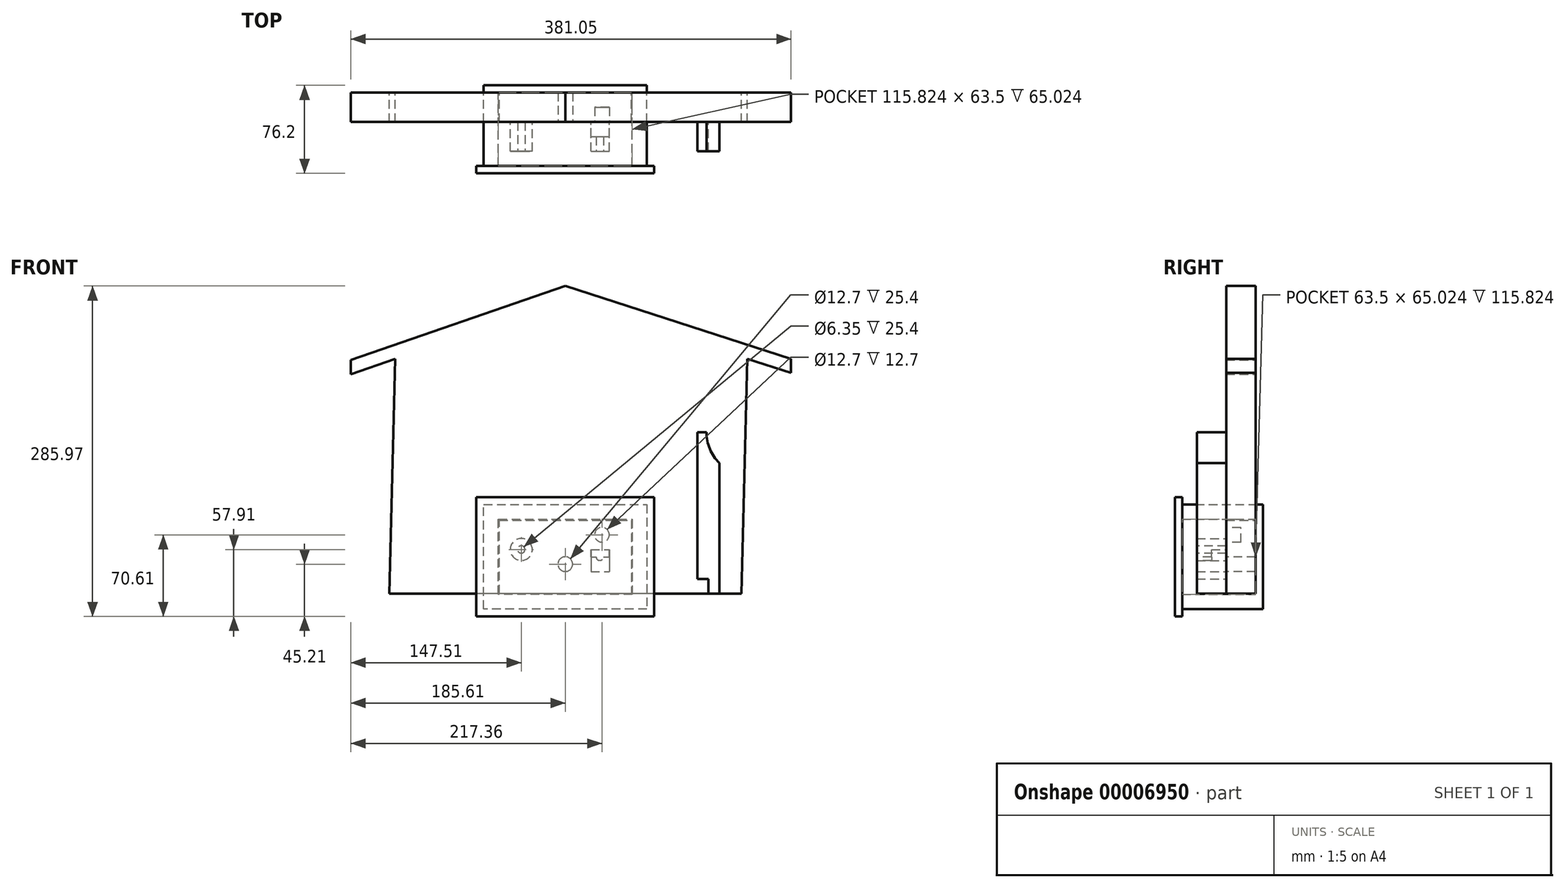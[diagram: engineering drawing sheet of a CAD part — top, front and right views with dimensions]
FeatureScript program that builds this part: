
annotation { "Feature Type Name" : "Feature", "Feature Type Description" : "" }
export const myFeature = defineFeature(function(context is Context, id is Id, definition is map)
    precondition{}
    {
        {
            var Q0;
            Q0=qCreatedBy(makeId("Front.planeOp"),FACE);
            var sketch = newSketch(context, id + "F0", { "sketchPlane" : qUnion([Q0])});
            skLineSegment(sketch, "E0", {"start": v(-57.15, 63.5) * mm, "end": v(57.15, 63.5) * mm});
            skLineSegment(sketch, "E1", {"start": v(57.15, 63.5) * mm, "end": v(57.15, 0) * mm});
            skLineSegment(sketch, "E2", {"start": v(57.15, 0) * mm, "end": v(-57.15, 0) * mm});
            skLineSegment(sketch, "E3", {"start": v(-57.15, 0) * mm, "end": v(-57.15, 63.5) * mm});
            skSolve(sketch);
        }
        {
            var Q0;
            Q0=makeQuery(id+"F0.imprint","IMPRINT",FACE,{"disambiguationData":[TD([[makeQuery(id+"F0.imprint","IMPRINT",EDGE,{"derivedFrom":sQuery(id+"F0.wireOp",EDGE,"E0")}),-1.0]])]});
            extrude(context, id + "F1", {"entities" : qUnion([Q0]), "depth" : 25.4 * mm});
        }
        {
            var Q0;
            Q0=makeQuery(id+"F1.opExtrude","CAP_FACE",FACE,{"disambiguationData":[OSD([sQuery(id+"F0.wireOp",EDGE,"E0"),sQuery(id+"F0.wireOp",EDGE,"E1"),sQuery(id+"F0.wireOp",EDGE,"E2"),sQuery(id+"F0.wireOp",EDGE,"E3")])],"isStart":false});
            var sketch = newSketch(context, id + "F2", { "sketchPlane" : qUnion([Q0])});
            skCircle(sketch, "E4", {"center": v(0, 25.4) * mm, "radius": 6.35 * mm});
            skSolve(sketch);
        }
        {
            var Q0;
            Q0 = qSketchRegion(id + "F2", true);
            extrude(context, id + "F3", {"entities" : qUnion([Q0]), "operationType" : NewBodyOperationType.REMOVE, "endBound" : BoundingType.UP_TO_NEXT, "oppositeDirection" : true, "depth" : 25.4 * mm});
        }
        {
            var Q0;
            Q0=makeQuery(id+"F1.opExtrude","CAP_FACE",FACE,{"disambiguationData":[OSD([sQuery(id+"F0.wireOp",EDGE,"E0"),sQuery(id+"F0.wireOp",EDGE,"E1"),sQuery(id+"F0.wireOp",EDGE,"E2"),sQuery(id+"F0.wireOp",EDGE,"E3")])],"isStart":false});
            var sketch = newSketch(context, id + "F4", { "sketchPlane" : qUnion([Q0])});
            skCircle(sketch, "E5", {"center": v(-38.1, 38.1) * mm, "radius": 9.53 * mm});
            skSolve(sketch);
        }
        {
            var Q0;
            Q0 = qSketchRegion(id + "F4", true);
            extrude(context, id + "F5", {"entities" : qUnion([Q0]), "operationType" : NewBodyOperationType.ADD, "depth" : 25.4 * mm});
        }
        {
            var Q0;
            Q0=makeQuery(id+"F1.opExtrude","CAP_FACE",FACE,{"disambiguationData":[OSD([sQuery(id+"F0.wireOp",EDGE,"E0"),sQuery(id+"F0.wireOp",EDGE,"E1"),sQuery(id+"F0.wireOp",EDGE,"E2"),sQuery(id+"F0.wireOp",EDGE,"E3")])],"isStart":false});
            var sketch = newSketch(context, id + "F6", { "sketchPlane" : qUnion([Q0])});
            skLineSegment(sketch, "E6.bottom", {"start": v(22.22, 38.1) * mm, "end": v(38.1, 38.1) * mm});
            skLineSegment(sketch, "E6.top", {"start": v(22.22, 19.05) * mm, "end": v(38.1, 19.05) * mm});
            skLineSegment(sketch, "E6.left", {"start": v(22.22, 38.1) * mm, "end": v(22.22, 19.05) * mm});
            skLineSegment(sketch, "E6.right", {"start": v(38.1, 38.1) * mm, "end": v(38.1, 19.05) * mm});
            skSolve(sketch);
        }
        {
            var Q0;
            Q0 = qSketchRegion(id + "F6", true);
            extrude(context, id + "F7", {"entities" : qUnion([Q0]), "depth" : 25.4 * mm});
        }
        {
            var Q0;
            Q0=makeQuery(id+"F5.opExtrude","CAP_FACE",FACE,{"disambiguationData":[OSD([sQuery(id+"F4.wireOp",EDGE,"E5")])],"isStart":false});
            var sketch = newSketch(context, id + "F8", { "sketchPlane" : qUnion([Q0])});
            skCircle(sketch, "E7", {"center": v(-38.1, 38.1) * mm, "radius": 3.18 * mm});
            skSolve(sketch);
        }
        {
            var Q0;
            Q0 = qSketchRegion(id + "F8", true);
            extrude(context, id + "F9", {"entities" : qUnion([Q0]), "operationType" : NewBodyOperationType.REMOVE, "oppositeDirection" : true, "depth" : 25.4 * mm});
        }
        {
            var Q0;
            Q0=makeQuery(id+"F1.opExtrude","CAP_FACE",FACE,{"disambiguationData":[OSD([sQuery(id+"F0.wireOp",EDGE,"E0"),sQuery(id+"F0.wireOp",EDGE,"E1"),sQuery(id+"F0.wireOp",EDGE,"E2"),sQuery(id+"F0.wireOp",EDGE,"E3")])],"isStart":true});
            var sketch = newSketch(context, id + "F10", { "sketchPlane" : qUnion([Q0])});
            skLineSegment(sketch, "E8.0", {"start": v(57.91, 64.26) * mm, "end": v(-57.91, 64.26) * mm});
            skLineSegment(sketch, "E8.1", {"start": v(57.91, -0.76) * mm, "end": v(57.91, 64.26) * mm});
            skLineSegment(sketch, "E8.2", {"start": v(-57.91, -0.76) * mm, "end": v(57.91, -0.76) * mm});
            skLineSegment(sketch, "E8.3", {"start": v(-57.91, 64.26) * mm, "end": v(-57.91, -0.76) * mm});
            skLineSegment(sketch, "E9.0", {"start": v(70.61, 76.96) * mm, "end": v(-70.61, 76.96) * mm});
            skLineSegment(sketch, "E9.1", {"start": v(70.61, -13.46) * mm, "end": v(70.61, 76.96) * mm});
            skLineSegment(sketch, "E9.2", {"start": v(-70.61, -13.46) * mm, "end": v(70.61, -13.46) * mm});
            skLineSegment(sketch, "E9.3", {"start": v(-70.61, 76.96) * mm, "end": v(-70.61, -13.46) * mm});
            skSolve(sketch);
        }
        {
            var Q0;
            Q0=makeQuery(id+"F10.imprint","IMPRINT",FACE,{"disambiguationData":[TD([[makeQuery(id+"F10.imprint","IMPRINT",EDGE,{"derivedFrom":sQuery(id+"F10.wireOp",EDGE,"E8.0")}),-1.0]])]});
            extrude(context, id + "F11", {"entities" : qUnion([Q0]), "oppositeDirection" : true, "depth" : 63.5 * mm});
        }
        {
            var Q0;
            Q0=makeQuery(id+"F11.opExtrude","CAP_FACE",FACE,{"disambiguationData":[OSD([sQuery(id+"F10.wireOp",EDGE,"E8.0"),sQuery(id+"F10.wireOp",EDGE,"E8.1"),sQuery(id+"F10.wireOp",EDGE,"E8.2"),sQuery(id+"F10.wireOp",EDGE,"E8.3"),sQuery(id+"F10.wireOp",EDGE,"E9.0"),sQuery(id+"F10.wireOp",EDGE,"E9.1"),sQuery(id+"F10.wireOp",EDGE,"E9.2"),sQuery(id+"F10.wireOp",EDGE,"E9.3")])],"isStart":true});
            extrude(context, id + "F12", {"entities" : qUnion([Q0]), "operationType" : NewBodyOperationType.ADD, "depth" : 6.35 * mm});
        }
        {
            var Q0;
            Q0=makeQuery(id+"F12.opExtrude","CAP_FACE",FACE,{"disambiguationData":[OSD([sQuery(id+"F10.wireOp",EDGE,"E8.0"),sQuery(id+"F10.wireOp",EDGE,"E8.1"),sQuery(id+"F10.wireOp",EDGE,"E8.2"),sQuery(id+"F10.wireOp",EDGE,"E8.3"),sQuery(id+"F10.wireOp",EDGE,"E9.0"),sQuery(id+"F10.wireOp",EDGE,"E9.1"),sQuery(id+"F10.wireOp",EDGE,"E9.2"),sQuery(id+"F10.wireOp",EDGE,"E9.3")])],"isStart":false});
            var sketch = newSketch(context, id + "F13", { "sketchPlane" : qUnion([Q0])});
            skLineSegment(sketch, "E10.0", {"start": v(57.91, 64.26) * mm, "end": v(-57.91, 64.26) * mm});
            skLineSegment(sketch, "E11.0", {"start": v(-57.91, 64.26) * mm, "end": v(-57.91, -0.76) * mm});
            skLineSegment(sketch, "E12.0", {"start": v(-57.91, -0.76) * mm, "end": v(57.91, -0.76) * mm});
            skLineSegment(sketch, "E13.0", {"start": v(57.91, -0.76) * mm, "end": v(57.91, 64.26) * mm});
            skSolve(sketch);
        }
        {
            var Q0;
            Q0=makeQuery(id+"F13.imprint","IMPRINT",FACE,{"disambiguationData":[TD([[makeQuery(id+"F13.imprint","IMPRINT",EDGE,{"derivedFrom":sQuery(id+"F13.wireOp",EDGE,"E10.0")}),1.0]])]});
            extrude(context, id + "F14", {"entities" : qUnion([Q0]), "operationType" : NewBodyOperationType.ADD, "oppositeDirection" : true, "depth" : 6.35 * mm});
        }
        {
            var Q0;
            Q0=makeQuery(id+"F11.opExtrude","CAP_FACE",FACE,{"disambiguationData":[OSD([sQuery(id+"F10.wireOp",EDGE,"E8.0"),sQuery(id+"F10.wireOp",EDGE,"E8.1"),sQuery(id+"F10.wireOp",EDGE,"E8.2"),sQuery(id+"F10.wireOp",EDGE,"E8.3"),sQuery(id+"F10.wireOp",EDGE,"E9.0"),sQuery(id+"F10.wireOp",EDGE,"E9.1"),sQuery(id+"F10.wireOp",EDGE,"E9.2"),sQuery(id+"F10.wireOp",EDGE,"E9.3")])],"isStart":false});
            var sketch = newSketch(context, id + "F15", { "sketchPlane" : qUnion([Q0])});
            skLineSegment(sketch, "E14.0", {"start": v(-76.96, 83.31) * mm, "end": v(76.96, 83.31) * mm});
            skLineSegment(sketch, "E14.1", {"start": v(-76.96, -19.81) * mm, "end": v(-76.96, 83.31) * mm});
            skLineSegment(sketch, "E14.2", {"start": v(76.96, -19.81) * mm, "end": v(-76.96, -19.81) * mm});
            skLineSegment(sketch, "E14.3", {"start": v(76.96, 83.31) * mm, "end": v(76.96, -19.81) * mm});
            skSolve(sketch);
        }
        {
            var Q0;
            Q0 = qSketchRegion(id + "F15", true);
            extrude(context, id + "F16", {"entities" : qUnion([Q0]), "operationType" : NewBodyOperationType.ADD, "depth" : 6.35 * mm});
        }
        {
            var Q0;
            Q0=makeQuery(id+"F1.opExtrude","CAP_FACE",FACE,{"disambiguationData":[OSD([sQuery(id+"F0.wireOp",EDGE,"E0"),sQuery(id+"F0.wireOp",EDGE,"E1"),sQuery(id+"F0.wireOp",EDGE,"E2"),sQuery(id+"F0.wireOp",EDGE,"E3")])],"isStart":false});
            var sketch = newSketch(context, id + "F17", { "sketchPlane" : qUnion([Q0])});
            skCircle(sketch, "E15", {"center": v(31.75, 50.8) * mm, "radius": 6.35 * mm});
            skSolve(sketch);
        }
        {
            var Q0;
            Q0 = qSketchRegion(id + "F17", true);
            extrude(context, id + "F18", {"entities" : qUnion([Q0]), "operationType" : NewBodyOperationType.REMOVE, "oppositeDirection" : true, "depth" : 12.7 * mm});
        }
        {
            var Q0;
            Q0=makeQuery(id+"F7.opExtrude","CAP_FACE",FACE,{"disambiguationData":[OSD([sQuery(id+"F6.wireOp",EDGE,"E6.bottom"),sQuery(id+"F6.wireOp",EDGE,"E6.top"),sQuery(id+"F6.wireOp",EDGE,"E6.left"),sQuery(id+"F6.wireOp",EDGE,"E6.right")])],"isStart":false});
            var sketch = newSketch(context, id + "F19", { "sketchPlane" : qUnion([Q0])});
            skCircle(sketch, "E16", {"center": v(29.84, 31.75) * mm, "radius": 3.18 * mm});
            skSolve(sketch);
        }
        {
            var Q0;
            Q0=makeQuery(id+"F19.imprint","IMPRINT",FACE,{"disambiguationData":[TD([[makeQuery(id+"F19.imprint","IMPRINT",EDGE,{"derivedFrom":sQuery(id+"F19.wireOp",EDGE,"E16")}),1.0]])]});
            extrude(context, id + "F20", {"entities" : qUnion([Q0]), "operationType" : NewBodyOperationType.REMOVE, "oppositeDirection" : true, "depth" : 12.7 * mm});
        }
        {
            var Q0;
            Q0=makeQuery(id+"F7.opExtrude","SWEPT_FACE",FACE,{"disambiguationData":[OSD([sQuery(id+"F6.wireOp",EDGE,"E6.bottom")])]});
            var sketch = newSketch(context, id + "F30", { "sketchPlane" : qUnion([Q0])});
            skLineSegment(sketch, "E17", {"start": v(22.22, -38.1) * mm, "end": v(38.1, -38.1) * mm});
            skLineSegment(sketch, "E18", {"start": v(38.1, -38.1) * mm, "end": v(38.1, -50.8) * mm});
            skLineSegment(sketch, "E19", {"start": v(38.1, -50.8) * mm, "end": v(22.22, -50.8) * mm});
            skLineSegment(sketch, "E20", {"start": v(22.22, -38.1) * mm, "end": v(22.22, -50.8) * mm});
            skSolve(sketch);
        }
        {
            var Q0;
            Q0=makeQuery(id+"F30.imprint","IMPRINT",FACE,{"disambiguationData":[TD([[makeQuery(id+"F30.imprint","IMPRINT",EDGE,{"derivedFrom":sQuery(id+"F30.wireOp",EDGE,"E17")}),-1.0]])]});
            extrude(context, id + "F21", {"entities" : qUnion([Q0]), "operationType" : NewBodyOperationType.REMOVE, "oppositeDirection" : true, "depth" : 6.35 * mm});
        }
        {
            var Q0;
            Q0=qCreatedBy(makeId("Front.planeOp"),FACE);
            var sketch = newSketch(context, id + "F22", { "sketchPlane" : qUnion([Q0])});
            skLineSegment(sketch, "E21.bottom", {"start": v(152.35, 0) * mm, "end": v(-152.45, 0) * mm});
            skLineSegment(sketch, "E21.top", {"start": v(157.65, 203.13) * mm, "end": v(-147.15, 203.13) * mm});
            skLineSegment(sketch, "E21.left", {"start": v(152.35, 0) * mm, "end": v(157.65, 203.13) * mm});
            skLineSegment(sketch, "E21.right", {"start": v(-152.45, 0) * mm, "end": v(-147.15, 203.13) * mm});
            skLineSegment(sketch, "E22", {"start": v(0, 253.93) * mm, "end": v(-185.61, 189.85) * mm});
            skLineSegment(sketch, "E23", {"start": v(0, 253.93) * mm, "end": v(195.44, 190.95) * mm});
            skLineSegment(sketch, "E24", {"start": v(-185.61, 189.85) * mm, "end": v(-185.61, 202.09) * mm});
            skLineSegment(sketch, "E25", {"start": v(-185.61, 202.09) * mm, "end": v(0, 266.16) * mm});
            skLineSegment(sketch, "E26", {"start": v(0, 266.16) * mm, "end": v(0, 253.93) * mm});
            skLineSegment(sketch, "E27", {"start": v(0, 266.16) * mm, "end": v(195.44, 203.18) * mm});
            skLineSegment(sketch, "E28", {"start": v(195.44, 203.18) * mm, "end": v(195.44, 190.95) * mm});
            skSolve(sketch);
        }
        {
            var Q0;
            Q0=makeQuery(id+"F22.imprint","IMPRINT",FACE,{"disambiguationData":[TD([[makeQuery(id+"F22.imprint","IMPRINT",EDGE,{"derivedFrom":sQuery(id+"F22.wireOp",EDGE,"E21.bottom")}),-1.0]])]});
            var Q1;
            {var subQ3=sQuery(id+"F22.wireOp",EDGE,"E21.top");Q1=makeQuery(id+"F22.imprint","IMPRINT",FACE,{"disambiguationData":[TD([[makeQuery(id+"F22.imprint","IMPRINT",EDGE,{"derivedFrom":subQ3}),-1.0]])]});}
            var Q2;
            {var subQ1=sQuery(id+"F22.wireOp",EDGE,"E24");Q2=makeQuery(id+"F22.imprint","IMPRINT",FACE,{"disambiguationData":[TD([[makeQuery(id+"F22.imprint","IMPRINT",EDGE,{"derivedFrom":subQ1}),-1.0]])]});}
            var Q3;
            {var subQ1=sQuery(id+"F22.wireOp",EDGE,"E26");Q3=makeQuery(id+"F22.imprint","IMPRINT",FACE,{"disambiguationData":[TD([[makeQuery(id+"F22.imprint","IMPRINT",EDGE,{"derivedFrom":subQ1}),1.0]])]});}
            extrude(context, id + "F31", {"entities" : qUnion([Q0, Q1, Q2, Q3]), "depth" : 25.4 * mm, "offsetDistance" : 25.4 * mm});
        }
        {
            var Q0;
            Q0=makeQuery(id+"F31.opExtrude","CAP_FACE",FACE,{"disambiguationData":[OSD([sQuery(id+"F22.wireOp",EDGE,"E21.bottom"),sQuery(id+"F22.wireOp",EDGE,"E21.left"),sQuery(id+"F22.wireOp",EDGE,"E21.right"),sQuery(id+"F22.wireOp",EDGE,"E22"),sQuery(id+"F22.wireOp",EDGE,"E23"),sQuery(id+"F22.wireOp",EDGE,"E24"),sQuery(id+"F22.wireOp",EDGE,"E25"),sQuery(id+"F22.wireOp",EDGE,"E27"),sQuery(id+"F22.wireOp",EDGE,"E28")])],"isStart":false});
            var sketch = newSketch(context, id + "F23", { "sketchPlane" : qUnion([Q0])});
            skLineSegment(sketch, "E29", {"start": v(133.3, 0) * mm, "end": v(133.3, 112.8) * mm});
            skLineSegment(sketch, "E30", {"start": v(133.3, 0) * mm, "end": v(123.77, 0) * mm});
            skLineSegment(sketch, "E31", {"start": v(123.77, 0) * mm, "end": v(123.77, 12.7) * mm});
            skLineSegment(sketch, "E32", {"start": v(123.77, 12.7) * mm, "end": v(114.25, 12.7) * mm});
            skLineSegment(sketch, "E33", {"start": v(114.25, 12.7) * mm, "end": v(114.25, 139.7) * mm});
            skLineSegment(sketch, "E34", {"start": v(114.25, 139.7) * mm, "end": v(122.19, 139.7) * mm});
            skArc(sketch, "E35", {"start": v(122.19, 139.7) * mm, "mid": v(125.07, 125.15) * mm, "end": v(133.3, 112.8) * mm});
            skSolve(sketch);
        }
        {
            var Q0;
            Q0=makeQuery(id+"F23.imprint","IMPRINT",FACE,{"disambiguationData":[TD([[makeQuery(id+"F23.imprint","IMPRINT",EDGE,{"derivedFrom":sQuery(id+"F23.wireOp",EDGE,"E29")}),1.0]])]});
            extrude(context, id + "F24", {"entities" : qUnion([Q0]), "depth" : 25.4 * mm});
        }
    });
